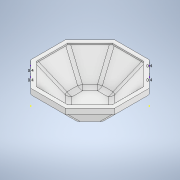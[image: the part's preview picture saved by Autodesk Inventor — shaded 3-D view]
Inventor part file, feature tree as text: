
AUTODESK INVENTOR PART (.ipt)
format: ipt  version: 2020.2 (Build 242310000, 310)  size: 206,848 bytes
history: native  units: in
note: dims shown in document units (in); Inventor stores cm internally (conversion verified against a paired STEP export)
features: sketch x6, extrude x2, chamfer x2, fillet x2
ambient origin geometry x8: Origin, YZ Plane, XZ Plane, XY Plane, X Axis, Y Axis, Z Axis, Center Point
bodies: Solid1 (feature_tree)
feature tree (12):
  extrude  "Extrusion1"  Depth=3.937in TaperAngle=0.0deg
  extrude  "Extrusion2"  Depth=3.3465in TaperAngle=0.0deg
  chamfer  "Chamfer1"  Distance=3.1496in Angle=45.0deg
  chamfer  "Chamfer2"  Distance=3.1496in Angle=45.0deg
  fillet  "Fillet1"  Radius=0.9843in
  fillet  "Fillet2"  Radius=0.9843in
  sketch  "Sketch3"  dims[d14=0.1575in]
  sketch  "Sketch4"  dims[d15=0.1575in]
  sketch  "Sketch5"  dims[d16=0.1575in]
  sketch  "Sketch6"  dims[d17=0.1575in]
  sketch  "Sketch1"  dims[d0=11.9291in d1=3.937in d2=0.0in]
  sketch  "Sketch2"  dims[d3=10.748in d4=3.3465in d5=0.0in d6=3.1496in d7=0.0492in d8=45.0deg d9=3.1496in d10=0.0492in d11=45.0deg d12=0.9843in d13=0.9843in]
